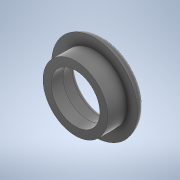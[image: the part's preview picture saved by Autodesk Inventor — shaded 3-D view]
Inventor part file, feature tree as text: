
AUTODESK INVENTOR PART (.ipt)
format: ipt  version: 2020 (Build 240168000, 168)  size: 324,096 bytes
history: native  units: mm
features: chamfer x3, fillet x3, revolve x1, sketch x1
ambient origin geometry x8: Origin, YZ Plane, XZ Plane, XY Plane, X Axis, Y Axis, Z Axis, Center Point
bodies: Volumenkörper1 (feature_tree)
feature tree (8):
  revolve  "Umdrehung1"
  chamfer  "Fase1"  Distance=5.1mm
  chamfer  "Fase2"  Distance=1.0mm
  chamfer  "Fase3"  Distance=9.0mm
  fillet  "Rundung1"  Radius=3.0mm
  fillet  "Rundung2"  Radius=2.0mm
  fillet  "Rundung3"  Radius=4.0mm
  sketch  "Skizze1"  dims[d0=6.8mm d1=5.1mm d2=1.0mm d3=9.0mm d4=3.0mm d5=2.0mm d6=4.0mm d7=90.0deg d8=1.0mm d9=2.0mm d10=45.0deg d11=1.25mm d12=2.0mm d13=45.0deg d14=2.25mm d15=2.0mm d16=45.0deg d17=5.25mm d18=1.5mm d19=1.5mm]
